# Revit family: FU_Modular_Sandler_Pau 1840PT
name_source: partatom
category: Furniture
units: mm (PartAtom-declared; Revit-internal decimal feet)

## family parameters
Always vertical = Yes
Cut with Voids When Loaded = No
OmniClass Number = 23.40.20.00
OmniClass Title = General Furniture and Specialties
Room Calculation Point = No
Shared = No
Work Plane-Based = No

## types (1)
- PAU1840PT
    Default Elevation = 0 mm  [stored 0 ft]
    Description = Upholstered rear privacy screen for sofas and modules with backrest.
    Manufacturer = Sandler
    Model = PAU1840PT
    Overall Elevation = 1300 mm  [stored 4.26509 ft]
    Panel Height = 1200 mm
    Thickness = 50 mm  [stored 0.164042 ft]
    URL = https://www.sandlerseating.com
    Width = 1600 mm  [stored 5.24934 ft]

note: [stored X ft] marks values corroborated as IEEE doubles in the binary element streams (Revit-internal decimal feet)

## geometry (parser evidence)
native form markers: Sweep x2
no freeform markers — native parametric forms only
